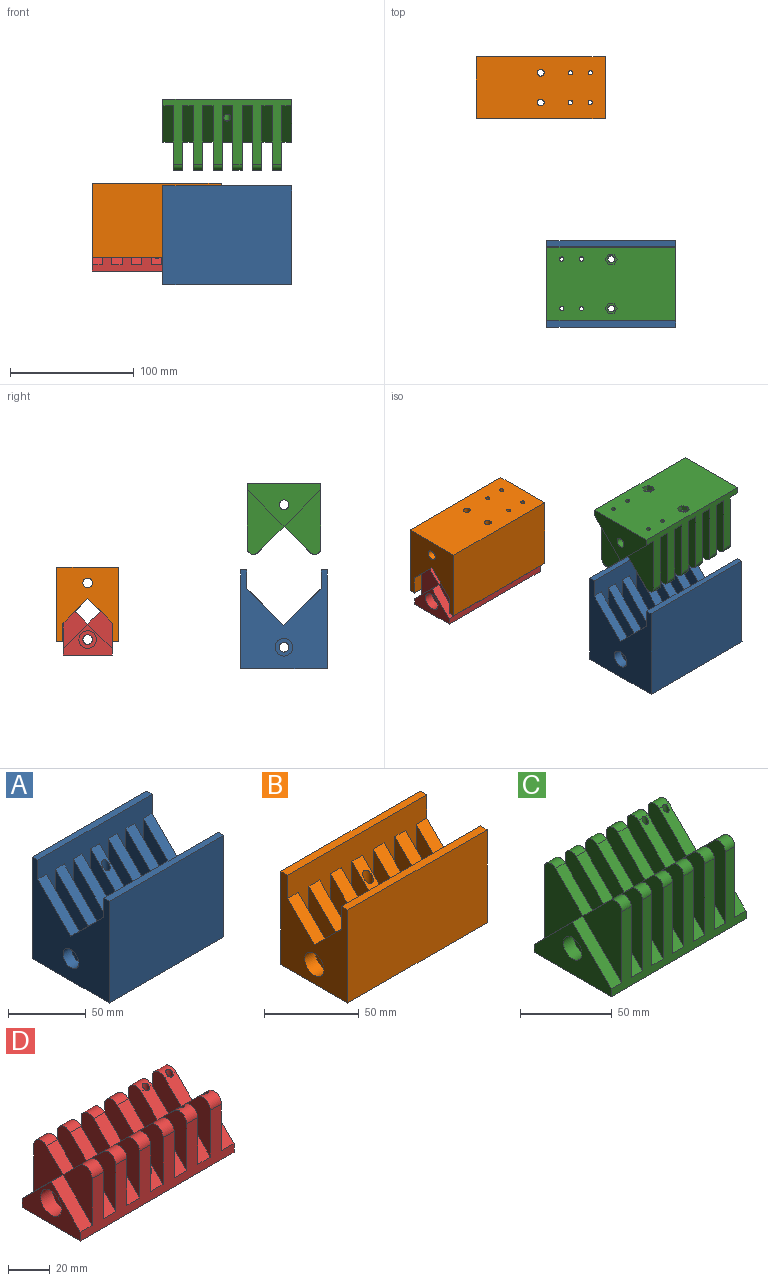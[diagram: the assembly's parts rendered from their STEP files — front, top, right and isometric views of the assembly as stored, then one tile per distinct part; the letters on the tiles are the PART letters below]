
ASSEMBLY  parts=4 mates=4
PART A: 68 faces, bbox 105.2x71.2x81.2 mm
  f0: plane 80x70mm, normal (-1,0,0), area 3640.5mm2, adj f1,f2,f4,f48,f49,f50,f51,f52
  f1: plane 104x70mm, normal (0,0,-1), area 7194mm2, adj f0,f50,f52,f56,f59,f60,f61,f62
  f2: plane 30x30mm, normal (0,-0.71,0.71), area 339.4mm2, adj f0,f3,f4,f48
  f3: plane 60x30mm, normal (1,0,0), area 900mm2, adj f2,f37,f48
  f4: plane 30x30mm, normal (0,0.71,0.71), area 339.4mm2, adj f0,f2,f5,f51
  f5: plane 60x30mm, normal (1,0,0), area 900mm2, adj f4,f36,f51
  f6: plane 30x30mm, normal (0,-0.71,0.71), area 339.4mm2, adj f7,f8,f9,f48
  f7: plane 60x30mm, normal (1,0,0), area 900mm2, adj f6,f39,f48
  f8: plane 60x30mm, normal (-1,0,0), area 900mm2, adj f6,f37,f48
  f9: plane 30x30mm, normal (0,0.71,0.71), area 339.4mm2, adj f6,f10,f11,f51
  f10: plane 60x30mm, normal (1,0,0), area 900mm2, adj f9,f38,f51
  f11: plane 60x30mm, normal (-1,0,0), area 900mm2, adj f9,f36,f51
  f12: plane 30x30mm, normal (0,-0.71,0.71), area 339.4mm2, adj f13,f14,f15,f48
  f13: plane 60x30mm, normal (1,0,0), area 900mm2, adj f12,f41,f48
  f14: plane 60x30mm, normal (-1,0,0), area 900mm2, adj f12,f39,f48
  f15: plane 30x30mm, normal (0,0.71,0.71), area 339.4mm2, adj f12,f16,f17,f51
  f16: plane 60x30mm, normal (1,0,0), area 900mm2, adj f15,f40,f51
  f17: plane 60x30mm, normal (-1,0,0), area 900mm2, adj f15,f38,f51
  f18: plane 31.16x31.16mm, normal (0,-0.71,0.71), area 305.8mm2, adj f19,f20,f21,f48,f64
  f19: plane 60x30mm, normal (1,0,0), area 900mm2, adj f18,f43,f48
  f20: plane 60x30mm, normal (-1,0,0), area 900mm2, adj f18,f41,f48
  f21: plane 31.16x31.16mm, normal (0,0.71,0.71), area 305.8mm2, adj f18,f22,f23,f51,f63
  f22: plane 60x30mm, normal (1,0,0), area 900mm2, adj f21,f42,f51
  f23: plane 60x30mm, normal (-1,0,0), area 900mm2, adj f21,f40,f51
  f24: plane 30x30mm, normal (0,-0.71,0.71), area 339.4mm2, adj f25,f26,f27,f48
  f25: plane 60x30mm, normal (1,0,0), area 900mm2, adj f24,f45,f48
  f26: plane 60x30mm, normal (-1,0,0), area 900mm2, adj f24,f43,f48
  f27: plane 30x30mm, normal (0,0.71,0.71), area 339.4mm2, adj f24,f28,f29,f51
  f28: plane 60x30mm, normal (1,0,0), area 900mm2, adj f27,f44,f51
  f29: plane 60x30mm, normal (-1,0,0), area 900mm2, adj f27,f42,f51
  f30: plane 30x30mm, normal (0,-0.71,0.71), area 339.4mm2, adj f31,f32,f33,f48
  f31: plane 60x30mm, normal (1,0,0), area 900mm2, adj f30,f47,f48
  f32: plane 60x30mm, normal (-1,0,0), area 900mm2, adj f30,f45,f48
  f33: plane 30x30mm, normal (0,0.71,0.71), area 339.4mm2, adj f30,f34,f35,f51
  f34: plane 60x30mm, normal (1,0,0), area 900mm2, adj f33,f46,f51
  f35: plane 60x30mm, normal (-1,0,0), area 900mm2, adj f33,f44,f51
  f36: plane 30.74x30.74mm, normal (0,-0.71,0.71), area 325.8mm2, adj f5,f11,f37,f51,f62
  f37: plane 30.74x30.74mm, normal (0,0.71,0.71), area 325.8mm2, adj f3,f8,f36,f48,f61
  f38: plane 30.74x30.74mm, normal (0,-0.71,0.71), area 325.8mm2, adj f10,f17,f39,f51,f60
  f39: plane 30.74x30.74mm, normal (0,0.71,0.71), area 325.8mm2, adj f7,f14,f38,f48,f59
  f40: plane 30x30mm, normal (0,-0.71,0.71), area 339.4mm2, adj f16,f23,f41,f51
  f41: plane 30x30mm, normal (0,0.71,0.71), area 339.4mm2, adj f13,f20,f40,f48
  f42: plane 30x30mm, normal (0,-0.71,0.71), area 339.4mm2, adj f22,f29,f43,f51
  f43: plane 30x30mm, normal (0,0.71,0.71), area 339.4mm2, adj f19,f26,f42,f48
  f44: plane 30x30mm, normal (0,-0.71,0.71), area 339.4mm2, adj f28,f35,f45,f51
  f45: plane 30x30mm, normal (0,0.71,0.71), area 339.4mm2, adj f25,f32,f44,f48
  f46: plane 30x30mm, normal (0,-0.71,0.71), area 339.4mm2, adj f34,f47,f51,f57
  f47: plane 30x30mm, normal (0,0.71,0.71), area 339.4mm2, adj f31,f46,f48,f54
  f48: plane 104x75mm, normal (0,-1,0), area 4440mm2, adj f0,f2,f3,f6,f7,f8,f12,f13
  f49: plane 104x5mm, normal (0,0,1), area 520mm2, adj f0,f48,f50,f56
  f50: plane 104x80mm, normal (0,1,0), area 8320mm2, adj f0,f1,f49,f56
  f51: plane 104x75mm, normal (0,1,0), area 4440mm2, adj f0,f4,f5,f9,f10,f11,f15,f16
  f52: plane 104x80mm, normal (0,-1,0), area 8320mm2, adj f0,f1,f53,f56
  f53: plane 104x5mm, normal (0,0,1), area 520mm2, adj f0,f51,f52,f56
  f54: plane 60x30mm, normal (-1,0,0), area 900mm2, adj f47,f48,f55
  f55: plane 30x30mm, normal (0,-0.71,0.71), area 339.4mm2, adj f48,f54,f56,f58
  f56: plane 80x70mm, normal (1,0,0), area 3752.2mm2, adj f1,f48,f49,f50,f51,f52,f53,f55
  f57: plane 60x30mm, normal (-1,0,0), area 900mm2, adj f46,f51,f58
  f58: plane 30x30mm, normal (0,0.71,0.71), area 339.4mm2, adj f51,f55,f56,f57
  f59: cylinder r=1.75mm len=16.85mm, axis (0,0,-1), area 166.5mm2, adj f1,f39
  f60: cylinder r=1.75mm len=16.76mm, axis (0,0,-1), area 165.6mm2, adj f1,f38
  f61: cylinder r=1.75mm len=16.76mm, axis (0,0,-1), area 165.6mm2, adj f1,f37
  f62: cylinder r=1.75mm len=16.76mm, axis (0,0,-1), area 165.6mm2, adj f1,f36
  f63: cylinder r=2.75mm len=57.76mm, axis (0,0,-1), area 952mm2, adj f1,f21
  f64: cylinder r=2.75mm len=57.76mm, axis (0,0,-1), area 952mm2, adj f1,f18
  f65: cylinder r=3.9mm len=96mm, axis (-1,0,0), area 2352.4mm2, adj f56,f66
  f66: plane 14.25x14.25mm, normal (-1,0,0), area 111.7mm2, adj f65,f67
  f67: cylinder r=7.12mm len=14.25mm, axis (-1,0,0), area 358.1mm2, adj f0,f66
PART B: 68 faces, bbox 105.2x51.2x61.2 mm
  f0: plane 60x50mm, normal (-1,0,0), area 1840.5mm2, adj f1,f2,f4,f48,f49,f50,f51,f52
  f1: plane 104x50mm, normal (0,0,-1), area 5114mm2, adj f0,f50,f52,f56,f59,f60,f61,f62
  f2: plane 20x20mm, normal (0,-0.71,0.71), area 226.3mm2, adj f0,f3,f4,f48
  f3: plane 40x20mm, normal (1,0,0), area 400mm2, adj f2,f37,f48
  f4: plane 20x20mm, normal (0,0.71,0.71), area 226.3mm2, adj f0,f2,f5,f51
  f5: plane 40x20mm, normal (1,0,0), area 400mm2, adj f4,f36,f51
  f6: plane 20x20mm, normal (0,-0.71,0.71), area 226.3mm2, adj f7,f8,f9,f48
  f7: plane 40x20mm, normal (1,0,0), area 400mm2, adj f6,f39,f48
  f8: plane 40x20mm, normal (-1,0,0), area 400mm2, adj f6,f37,f48
  f9: plane 20x20mm, normal (0,0.71,0.71), area 226.3mm2, adj f6,f10,f11,f51
  f10: plane 40x20mm, normal (1,0,0), area 400mm2, adj f9,f38,f51
  f11: plane 40x20mm, normal (-1,0,0), area 400mm2, adj f9,f36,f51
  f12: plane 20x20mm, normal (0,-0.71,0.71), area 226.3mm2, adj f13,f14,f15,f48
  f13: plane 40x20mm, normal (1,0,0), area 400mm2, adj f12,f41,f48
  f14: plane 40x20mm, normal (-1,0,0), area 400mm2, adj f12,f39,f48
  f15: plane 20x20mm, normal (0,0.71,0.71), area 226.3mm2, adj f12,f16,f17,f51
  f16: plane 40x20mm, normal (1,0,0), area 400mm2, adj f15,f40,f51
  f17: plane 40x20mm, normal (-1,0,0), area 400mm2, adj f15,f38,f51
  f18: plane 21.16x21.16mm, normal (0,-0.71,0.71), area 192.7mm2, adj f19,f20,f21,f48,f64
  f19: plane 40x20mm, normal (1,0,0), area 400mm2, adj f18,f43,f48
  f20: plane 40x20mm, normal (-1,0,0), area 400mm2, adj f18,f41,f48
  f21: plane 21.16x21.16mm, normal (0,0.71,0.71), area 192.7mm2, adj f18,f22,f23,f51,f63
  f22: plane 40x20mm, normal (1,0,0), area 400mm2, adj f21,f42,f51
  f23: plane 40x20mm, normal (-1,0,0), area 400mm2, adj f21,f40,f51
  f24: plane 20x20mm, normal (0,-0.71,0.71), area 226.3mm2, adj f25,f26,f27,f48
  f25: plane 40x20mm, normal (1,0,0), area 400mm2, adj f24,f45,f48
  f26: plane 40x20mm, normal (-1,0,0), area 400mm2, adj f24,f43,f48
  f27: plane 20x20mm, normal (0,0.71,0.71), area 226.3mm2, adj f24,f28,f29,f51
  f28: plane 40x20mm, normal (1,0,0), area 400mm2, adj f27,f44,f51
  f29: plane 40x20mm, normal (-1,0,0), area 400mm2, adj f27,f42,f51
  f30: plane 20x20mm, normal (0,-0.71,0.71), area 226.3mm2, adj f31,f32,f33,f48
  f31: plane 40x20mm, normal (1,0,0), area 400mm2, adj f30,f47,f48
  f32: plane 40x20mm, normal (-1,0,0), area 400mm2, adj f30,f45,f48
  f33: plane 20x20mm, normal (0,0.71,0.71), area 226.3mm2, adj f30,f34,f35,f51
  f34: plane 40x20mm, normal (1,0,0), area 400mm2, adj f33,f46,f51
  f35: plane 40x20mm, normal (-1,0,0), area 400mm2, adj f33,f44,f51
  f36: plane 20.74x20.74mm, normal (0,-0.71,0.71), area 212.7mm2, adj f5,f11,f37,f51,f62
  f37: plane 20.74x20.74mm, normal (0,0.71,0.71), area 212.7mm2, adj f3,f8,f36,f48,f61
  f38: plane 20.74x20.74mm, normal (0,-0.71,0.71), area 212.7mm2, adj f10,f17,f39,f51,f60
  f39: plane 20.74x20.74mm, normal (0,0.71,0.71), area 212.7mm2, adj f7,f14,f38,f48,f59
  f40: plane 20x20mm, normal (0,-0.71,0.71), area 226.3mm2, adj f16,f23,f41,f51
  f41: plane 20x20mm, normal (0,0.71,0.71), area 226.3mm2, adj f13,f20,f40,f48
  f42: plane 20x20mm, normal (0,-0.71,0.71), area 226.3mm2, adj f22,f29,f43,f51
  f43: plane 20x20mm, normal (0,0.71,0.71), area 226.3mm2, adj f19,f26,f42,f48
  f44: plane 20x20mm, normal (0,-0.71,0.71), area 226.3mm2, adj f28,f35,f45,f51
  f45: plane 20x20mm, normal (0,0.71,0.71), area 226.3mm2, adj f25,f32,f44,f48
  f46: plane 20x20mm, normal (0,-0.71,0.71), area 226.3mm2, adj f34,f47,f51,f57
  f47: plane 20x20mm, normal (0,0.71,0.71), area 226.3mm2, adj f31,f46,f48,f54
  f48: plane 104x55mm, normal (0,-1,0), area 3480mm2, adj f0,f2,f3,f6,f7,f8,f12,f13
  f49: plane 104x5mm, normal (0,0,1), area 520mm2, adj f0,f48,f50,f56
  f50: plane 104x60mm, normal (0,1,0), area 6240mm2, adj f0,f1,f49,f56
  f51: plane 104x55mm, normal (0,1,0), area 3480mm2, adj f0,f4,f5,f9,f10,f11,f15,f16
  f52: plane 104x60mm, normal (0,-1,0), area 6240mm2, adj f0,f1,f53,f56
  f53: plane 104x5mm, normal (0,0,1), area 520mm2, adj f0,f51,f52,f56
  f54: plane 40x20mm, normal (-1,0,0), area 400mm2, adj f47,f48,f55
  f55: plane 20x20mm, normal (0,-0.71,0.71), area 226.3mm2, adj f48,f54,f56,f58
  f56: plane 60x50mm, normal (1,0,0), area 1952.2mm2, adj f1,f48,f49,f50,f51,f52,f53,f55
  f57: plane 40x20mm, normal (-1,0,0), area 400mm2, adj f46,f51,f58
  f58: plane 20x20mm, normal (0,0.71,0.71), area 226.3mm2, adj f51,f55,f56,f57
  f59: cylinder r=1.75mm len=14.76mm, axis (0,0,-1), area 143.6mm2, adj f1,f39
  f60: cylinder r=1.75mm len=14.76mm, axis (0,0,-1), area 143.6mm2, adj f1,f38
  f61: cylinder r=1.75mm len=14.76mm, axis (0,0,-1), area 143.6mm2, adj f1,f37
  f62: cylinder r=1.75mm len=14.76mm, axis (0,0,-1), area 143.6mm2, adj f1,f36
  f63: cylinder r=2.75mm len=39.76mm, axis (0,0,-1), area 640.9mm2, adj f1,f21
  f64: cylinder r=2.75mm len=39.76mm, axis (0,0,-1), area 640.9mm2, adj f1,f18
  f65: cylinder r=3.9mm len=96mm, axis (-1,0,0), area 2352.4mm2, adj f56,f66
  f66: plane 14.25x14.25mm, normal (-1,0,0), area 111.7mm2, adj f65,f67
  f67: cylinder r=7.12mm len=14.25mm, axis (-1,0,0), area 358.1mm2, adj f0,f66
PART C: 90 faces, bbox 105.2x60.7x58.8 mm
  f0: cylinder r=5mm len=8.54mm, axis (1,0,0), area 87.1mm2, adj f19,f20,f21,f55,f70
  f1: cylinder r=5mm len=8.54mm, axis (1,0,0), area 87.1mm2, adj f22,f23,f24,f55,f69
  f2: cylinder r=5mm len=8.54mm, axis (-1,0,0), area 87.1mm2, adj f42,f43,f44,f54,f68
  f3: cylinder r=5mm len=8.54mm, axis (-1,0,0), area 87.1mm2, adj f45,f46,f47,f54,f67
  f4: plane 52.43x29.75mm, normal (-1,0,0), area 854.2mm2, adj f31,f54,f60,f65
  f5: plane 104x59.5mm, normal (0,0,-1), area 6033.1mm2, adj f7,f54,f55,f66,f67,f68,f69,f70
  f6: plane 52.43x29.75mm, normal (-1,0,0), area 854.2mm2, adj f8,f55,f56,f64
  f7: plane 59.5x35mm, normal (1,0,0), area 1149.7mm2, adj f5,f30,f53,f54,f55,f87
  f8: plane 21.21x21.21mm, normal (0,0.71,0.71), area 225mm2, adj f6,f9,f31,f56
  f9: plane 52.43x29.75mm, normal (1,0,0), area 854.2mm2, adj f8,f25,f55,f56
  f10: plane 21.21x21.21mm, normal (0,0.71,0.71), area 225mm2, adj f11,f12,f33,f57
  f11: plane 52.43x29.75mm, normal (1,0,0), area 854.2mm2, adj f10,f26,f55,f57
  f12: plane 52.43x29.75mm, normal (-1,0,0), area 854.2mm2, adj f10,f25,f55,f57
  f13: plane 21.21x21.21mm, normal (0,0.71,0.71), area 225mm2, adj f14,f15,f36,f58
  f14: plane 52.43x29.75mm, normal (1,0,0), area 854.2mm2, adj f13,f27,f55,f58
  f15: plane 52.43x29.75mm, normal (-1,0,0), area 854.2mm2, adj f13,f26,f55,f58
  f16: plane 21.21x21.21mm, normal (0,0.71,0.71), area 225mm2, adj f17,f18,f39,f59
  f17: plane 52.43x29.75mm, normal (1,0,0), area 854.2mm2, adj f16,f28,f55,f59
  f18: plane 52.43x29.75mm, normal (-1,0,0), area 854.2mm2, adj f16,f27,f55,f59
  f19: plane 21.31x21.31mm, normal (0,0.71,0.71), area 212.7mm2, adj f0,f20,f21,f42,f70
  f20: plane 52.43x29.75mm, normal (1,0,0), area 854.2mm2, adj f0,f19,f29,f55
  f21: plane 52.43x29.75mm, normal (-1,0,0), area 854.2mm2, adj f0,f19,f28,f55
  f22: plane 21.31x21.31mm, normal (0,0.71,0.71), area 212.7mm2, adj f1,f23,f24,f45,f69
  f23: plane 52.43x29.75mm, normal (1,0,0), area 854.2mm2, adj f1,f22,f30,f55
  f24: plane 52.43x29.75mm, normal (-1,0,0), area 854.2mm2, adj f1,f22,f29,f55
  f25: plane 29.75x29.75mm, normal (0,-0.71,0.71), area 357.6mm2, adj f9,f12,f48,f55
  f26: plane 29.75x29.75mm, normal (0,-0.71,0.71), area 357.6mm2, adj f11,f15,f49,f55
  f27: plane 30.91x30.91mm, normal (0,-0.71,0.71), area 324mm2, adj f14,f18,f50,f55,f85
  f28: plane 29.75x29.75mm, normal (0,-0.71,0.71), area 357.6mm2, adj f17,f21,f51,f55
  f29: plane 29.75x29.75mm, normal (0,-0.71,0.71), area 357.6mm2, adj f20,f24,f52,f55
  f30: plane 29.75x29.75mm, normal (0,-0.71,0.71), area 357.6mm2, adj f7,f23,f53,f55
  f31: plane 21.21x21.21mm, normal (0,-0.71,0.71), area 225mm2, adj f4,f8,f32,f60
  f32: plane 52.43x29.75mm, normal (1,0,0), area 854.2mm2, adj f31,f48,f54,f60
  f33: plane 21.21x21.21mm, normal (0,-0.71,0.71), area 225mm2, adj f10,f34,f35,f61
  f34: plane 52.43x29.75mm, normal (1,0,0), area 854.2mm2, adj f33,f49,f54,f61
  f35: plane 52.43x29.75mm, normal (-1,0,0), area 854.2mm2, adj f33,f48,f54,f61
  f36: plane 21.21x21.21mm, normal (0,-0.71,0.71), area 225mm2, adj f13,f37,f38,f62
  f37: plane 52.43x29.75mm, normal (1,0,0), area 854.2mm2, adj f36,f50,f54,f62
  f38: plane 52.43x29.75mm, normal (-1,0,0), area 854.2mm2, adj f36,f49,f54,f62
  f39: plane 21.21x21.21mm, normal (0,-0.71,0.71), area 225mm2, adj f16,f40,f41,f63
  f40: plane 52.43x29.75mm, normal (1,0,0), area 854.2mm2, adj f39,f51,f54,f63
  f41: plane 52.43x29.75mm, normal (-1,0,0), area 854.2mm2, adj f39,f50,f54,f63
  f42: plane 21.31x21.31mm, normal (0,-0.71,0.71), area 212.7mm2, adj f2,f19,f43,f44,f68
  f43: plane 52.43x29.75mm, normal (1,0,0), area 854.2mm2, adj f2,f42,f52,f54
  f44: plane 52.43x29.75mm, normal (-1,0,0), area 854.2mm2, adj f2,f42,f51,f54
  f45: plane 21.31x21.31mm, normal (0,-0.71,0.71), area 212.7mm2, adj f3,f22,f46,f47,f67
  f46: plane 52.43x29.75mm, normal (1,0,0), area 854.2mm2, adj f3,f45,f53,f54
  f47: plane 52.43x29.75mm, normal (-1,0,0), area 854.2mm2, adj f3,f45,f52,f54
  f48: plane 29.75x29.75mm, normal (0,0.71,0.71), area 357.6mm2, adj f25,f32,f35,f54
  f49: plane 29.75x29.75mm, normal (0,0.71,0.71), area 357.6mm2, adj f26,f34,f38,f54
  f50: plane 30.91x30.91mm, normal (0,0.71,0.71), area 324mm2, adj f27,f37,f41,f54,f86
  f51: plane 29.75x29.75mm, normal (0,0.71,0.71), area 357.6mm2, adj f28,f40,f44,f54
  f52: plane 29.75x29.75mm, normal (0,0.71,0.71), area 357.6mm2, adj f29,f43,f47,f54
  f53: plane 29.75x29.75mm, normal (0,0.71,0.71), area 357.6mm2, adj f7,f30,f46,f54
  f54: plane 104x52.68mm, normal (0,1,0), area 2680.3mm2, adj f2,f3,f4,f5,f7,f32,f34,f35
  f55: plane 104x52.68mm, normal (0,-1,0), area 2680.3mm2, adj f0,f1,f5,f6,f7,f9,f11,f12
  f56: cylinder r=5mm len=8.54mm, axis (1,0,0), area 88.4mm2, adj f6,f8,f9,f55
  f57: cylinder r=5mm len=8.54mm, axis (1,0,0), area 88.4mm2, adj f10,f11,f12,f55
  f58: cylinder r=5mm len=8.54mm, axis (1,0,0), area 88.4mm2, adj f13,f14,f15,f55
  f59: cylinder r=5mm len=8.54mm, axis (1,0,0), area 88.4mm2, adj f16,f17,f18,f55
  f60: cylinder r=5mm len=8.54mm, axis (-1,0,0), area 88.4mm2, adj f4,f31,f32,f54
  f61: cylinder r=5mm len=8.54mm, axis (-1,0,0), area 88.4mm2, adj f33,f34,f35,f54
  f62: cylinder r=5mm len=8.54mm, axis (-1,0,0), area 88.4mm2, adj f36,f37,f38,f54
  f63: cylinder r=5mm len=8.54mm, axis (-1,0,0), area 88.4mm2, adj f39,f40,f41,f54
  f64: plane 29.75x29.75mm, normal (0,-0.71,0.71), area 336.6mm2, adj f6,f55,f65,f66
  f65: plane 29.75x29.75mm, normal (0,0.71,0.71), area 336.6mm2, adj f4,f54,f64,f66
  f66: plane 59.5x35mm, normal (-1,0,0), area 1038mm2, adj f5,f54,f55,f64,f65,f89
  f67: cylinder r=1.75mm len=56.21mm, axis (0,0,-1), area 603.7mm2, adj f3,f5,f45
  f68: cylinder r=1.75mm len=56.21mm, axis (0,0,-1), area 603.7mm2, adj f2,f5,f42
  f69: cylinder r=1.75mm len=56.21mm, axis (0,0,-1), area 603.7mm2, adj f1,f5,f22
  f70: cylinder r=1.75mm len=56.21mm, axis (0,0,-1), area 603.7mm2, adj f0,f5,f19
  f71: plane 4.5x4.1mm, normal (-0.87,0.5,0), area 21.3mm2, adj f5,f72,f76,f77
  f72: plane 4.73x4.5mm, normal (0,1,0), area 21.3mm2, adj f5,f71,f73,f77
  f73: plane 4.5x4.1mm, normal (0.87,0.5,0), area 21.3mm2, adj f5,f72,f74,f77
  f74: plane 4.5x4.1mm, normal (0.87,-0.5,0), area 21.3mm2, adj f5,f73,f75,f77
  f75: plane 4.73x4.5mm, normal (0,-1,0), area 21.3mm2, adj f5,f74,f76,f77
  f76: plane 4.5x4.1mm, normal (-0.87,-0.5,0), area 21.3mm2, adj f5,f71,f75,f77
  f77: plane 9.47x8.2mm, normal (0,0,-1), area 34.5mm2, adj f71,f72,f73,f74,f75,f76,f86
  f78: plane 4.73x4.5mm, normal (0,1,0), area 21.3mm2, adj f5,f79,f83,f84
  f79: plane 4.5x4.1mm, normal (0.87,0.5,0), area 21.3mm2, adj f5,f78,f80,f84
  f80: plane 4.5x4.1mm, normal (0.87,-0.5,0), area 21.3mm2, adj f5,f79,f81,f84
  f81: plane 4.73x4.5mm, normal (0,-1,0), area 21.3mm2, adj f5,f80,f82,f84
  f82: plane 4.5x4.1mm, normal (-0.87,-0.5,0), area 21.3mm2, adj f5,f81,f83,f84
  f83: plane 4.5x4.1mm, normal (-0.87,0.5,0), area 21.3mm2, adj f5,f78,f82,f84
  f84: plane 9.47x8.2mm, normal (0,0,-1), area 34.5mm2, adj f78,f79,f80,f81,f82,f83,f85
  f85: cylinder r=2.75mm len=13.26mm, axis (0,0,-1), area 183mm2, adj f27,f84
  f86: cylinder r=2.75mm len=13.26mm, axis (0,0,-1), area 183mm2, adj f50,f77
  f87: cylinder r=3.9mm len=96mm, axis (-1,0,0), area 2352.4mm2, adj f7,f88
  f88: plane 14.25x14.25mm, normal (-1,0,0), area 111.7mm2, adj f87,f89
  f89: cylinder r=7.12mm len=14.25mm, axis (-1,0,0), area 358.1mm2, adj f66,f88
PART D: 90 faces, bbox 105.2x40.7x38.8 mm
  f0: cylinder r=5mm len=8.54mm, axis (1,0,0), area 79.7mm2, adj f19,f20,f21,f55,f70
  f1: cylinder r=5mm len=8.54mm, axis (1,0,0), area 79.7mm2, adj f22,f23,f24,f55,f69
  f2: cylinder r=5mm len=8.54mm, axis (-1,0,0), area 79.7mm2, adj f42,f43,f44,f54,f68
  f3: cylinder r=5mm len=8.54mm, axis (-1,0,0), area 79.7mm2, adj f45,f46,f47,f54,f67
  f4: plane 32.43x19.75mm, normal (-1,0,0), area 359.2mm2, adj f31,f54,f60,f65
  f5: plane 104x39.5mm, normal (0,0,-1), area 3953.1mm2, adj f7,f54,f55,f66,f67,f68,f69,f70
  f6: plane 32.43x19.75mm, normal (-1,0,0), area 359.2mm2, adj f8,f55,f56,f64
  f7: plane 39.5x25mm, normal (1,0,0), area 549.7mm2, adj f5,f30,f53,f54,f55,f87
  f8: plane 11.21x11.21mm, normal (0,0.71,0.71), area 118.9mm2, adj f6,f9,f31,f56
  f9: plane 32.43x19.75mm, normal (1,0,0), area 359.2mm2, adj f8,f25,f55,f56
  f10: plane 11.21x11.21mm, normal (0,0.71,0.71), area 118.9mm2, adj f11,f12,f33,f57
  f11: plane 32.43x19.75mm, normal (1,0,0), area 359.2mm2, adj f10,f26,f55,f57
  f12: plane 32.43x19.75mm, normal (-1,0,0), area 359.2mm2, adj f10,f25,f55,f57
  f13: plane 11.21x11.21mm, normal (0,0.71,0.71), area 118.9mm2, adj f14,f15,f36,f58
  f14: plane 32.43x19.75mm, normal (1,0,0), area 359.2mm2, adj f13,f27,f55,f58
  f15: plane 32.43x19.75mm, normal (-1,0,0), area 359.2mm2, adj f13,f26,f55,f58
  f16: plane 11.21x11.21mm, normal (0,0.71,0.71), area 118.9mm2, adj f17,f18,f39,f59
  f17: plane 32.43x19.75mm, normal (1,0,0), area 359.2mm2, adj f16,f28,f55,f59
  f18: plane 32.43x19.75mm, normal (-1,0,0), area 359.2mm2, adj f16,f27,f55,f59
  f19: plane 11.21x11.21mm, normal (0,0.71,0.71), area 115.9mm2, adj f0,f20,f21,f42,f70
  f20: plane 32.43x19.75mm, normal (1,0,0), area 359.2mm2, adj f0,f19,f29,f55
  f21: plane 32.43x19.75mm, normal (-1,0,0), area 359.2mm2, adj f0,f19,f28,f55
  f22: plane 11.21x11.21mm, normal (0,0.71,0.71), area 115.9mm2, adj f1,f23,f24,f45,f69
  f23: plane 32.43x19.75mm, normal (1,0,0), area 359.2mm2, adj f1,f22,f30,f55
  f24: plane 32.43x19.75mm, normal (-1,0,0), area 359.2mm2, adj f1,f22,f29,f55
  f25: plane 19.75x19.75mm, normal (0,-0.71,0.71), area 237.4mm2, adj f9,f12,f48,f55
  f26: plane 19.75x19.75mm, normal (0,-0.71,0.71), area 237.4mm2, adj f11,f15,f49,f55
  f27: plane 20.91x20.91mm, normal (0,-0.71,0.71), area 203.8mm2, adj f14,f18,f50,f55,f86
  f28: plane 19.75x19.75mm, normal (0,-0.71,0.71), area 237.4mm2, adj f17,f21,f51,f55
  f29: plane 19.75x19.75mm, normal (0,-0.71,0.71), area 237.4mm2, adj f20,f24,f52,f55
  f30: plane 19.75x19.75mm, normal (0,-0.71,0.71), area 237.4mm2, adj f7,f23,f53,f55
  f31: plane 11.21x11.21mm, normal (0,-0.71,0.71), area 118.9mm2, adj f4,f8,f32,f60
  f32: plane 32.43x19.75mm, normal (1,0,0), area 359.2mm2, adj f31,f48,f54,f60
  f33: plane 11.21x11.21mm, normal (0,-0.71,0.71), area 118.9mm2, adj f10,f34,f35,f61
  f34: plane 32.43x19.75mm, normal (1,0,0), area 359.2mm2, adj f33,f49,f54,f61
  f35: plane 32.43x19.75mm, normal (-1,0,0), area 359.2mm2, adj f33,f48,f54,f61
  f36: plane 11.21x11.21mm, normal (0,-0.71,0.71), area 118.9mm2, adj f13,f37,f38,f62
  f37: plane 32.43x19.75mm, normal (1,0,0), area 359.2mm2, adj f36,f50,f54,f62
  f38: plane 32.43x19.75mm, normal (-1,0,0), area 359.2mm2, adj f36,f49,f54,f62
  f39: plane 11.21x11.21mm, normal (0,-0.71,0.71), area 118.9mm2, adj f16,f40,f41,f63
  f40: plane 32.43x19.75mm, normal (1,0,0), area 359.2mm2, adj f39,f51,f54,f63
  f41: plane 32.43x19.75mm, normal (-1,0,0), area 359.2mm2, adj f39,f50,f54,f63
  f42: plane 11.21x11.21mm, normal (0,-0.71,0.71), area 115.9mm2, adj f2,f19,f43,f44,f68
  f43: plane 32.43x19.75mm, normal (1,0,0), area 359.2mm2, adj f2,f42,f52,f54
  f44: plane 32.43x19.75mm, normal (-1,0,0), area 359.2mm2, adj f2,f42,f51,f54
  f45: plane 11.21x11.21mm, normal (0,-0.71,0.71), area 115.9mm2, adj f3,f22,f46,f47,f67
  f46: plane 32.43x19.75mm, normal (1,0,0), area 359.2mm2, adj f3,f45,f53,f54
  f47: plane 32.43x19.75mm, normal (-1,0,0), area 359.2mm2, adj f3,f45,f52,f54
  f48: plane 19.75x19.75mm, normal (0,0.71,0.71), area 237.4mm2, adj f25,f32,f35,f54
  f49: plane 19.75x19.75mm, normal (0,0.71,0.71), area 237.4mm2, adj f26,f34,f38,f54
  f50: plane 20.91x20.91mm, normal (0,0.71,0.71), area 203.8mm2, adj f27,f37,f41,f54,f85
  f51: plane 19.75x19.75mm, normal (0,0.71,0.71), area 237.4mm2, adj f28,f40,f44,f54
  f52: plane 19.75x19.75mm, normal (0,0.71,0.71), area 237.4mm2, adj f29,f43,f47,f54
  f53: plane 19.75x19.75mm, normal (0,0.71,0.71), area 237.4mm2, adj f7,f30,f46,f54
  f54: plane 104x32.68mm, normal (0,1,0), area 1780.3mm2, adj f2,f3,f4,f5,f7,f32,f34,f35
  f55: plane 104x32.68mm, normal (0,-1,0), area 1780.3mm2, adj f0,f1,f5,f6,f7,f9,f11,f12
  f56: cylinder r=5mm len=8.54mm, axis (1,0,0), area 88.4mm2, adj f6,f8,f9,f55
  f57: cylinder r=5mm len=8.54mm, axis (1,0,0), area 88.4mm2, adj f10,f11,f12,f55
  f58: cylinder r=5mm len=8.54mm, axis (1,0,0), area 88.4mm2, adj f13,f14,f15,f55
  f59: cylinder r=5mm len=8.54mm, axis (1,0,0), area 88.4mm2, adj f16,f17,f18,f55
  f60: cylinder r=5mm len=8.54mm, axis (-1,0,0), area 88.4mm2, adj f4,f31,f32,f54
  f61: cylinder r=5mm len=8.54mm, axis (-1,0,0), area 88.4mm2, adj f33,f34,f35,f54
  f62: cylinder r=5mm len=8.54mm, axis (-1,0,0), area 88.4mm2, adj f36,f37,f38,f54
  f63: cylinder r=5mm len=8.54mm, axis (-1,0,0), area 88.4mm2, adj f39,f40,f41,f54
  f64: plane 19.75x19.75mm, normal (0,-0.71,0.71), area 223.4mm2, adj f6,f55,f65,f66
  f65: plane 19.75x19.75mm, normal (0,0.71,0.71), area 223.4mm2, adj f4,f54,f64,f66
  f66: plane 39.5x25mm, normal (-1,0,0), area 438mm2, adj f5,f54,f55,f64,f65,f89
  f67: cylinder r=1.75mm len=37.58mm, axis (0,0,-1), area 402.6mm2, adj f3,f5,f45
  f68: cylinder r=1.75mm len=37.58mm, axis (0,0,-1), area 402.6mm2, adj f2,f5,f42
  f69: cylinder r=1.75mm len=37.58mm, axis (0,0,-1), area 402.6mm2, adj f1,f5,f22
  f70: cylinder r=1.75mm len=37.58mm, axis (0,0,-1), area 402.6mm2, adj f0,f5,f19
  f71: plane 4.5x4.1mm, normal (-0.87,0.5,0), area 21.3mm2, adj f5,f72,f76,f77
  f72: plane 4.73x4.5mm, normal (0,1,0), area 21.3mm2, adj f5,f71,f73,f77
  f73: plane 4.5x4.1mm, normal (0.87,0.5,0), area 21.3mm2, adj f5,f72,f74,f77
  f74: plane 4.5x4.1mm, normal (0.87,-0.5,0), area 21.3mm2, adj f5,f73,f75,f77
  f75: plane 4.73x4.5mm, normal (0,-1,0), area 21.3mm2, adj f5,f74,f76,f77
  f76: plane 4.5x4.1mm, normal (-0.87,-0.5,0), area 21.3mm2, adj f5,f71,f75,f77
  f77: plane 9.47x8.2mm, normal (0,0,-1), area 34.5mm2, adj f71,f72,f73,f74,f75,f76,f85
  f78: plane 4.73x4.5mm, normal (0,1,0), area 21.3mm2, adj f5,f79,f83,f84
  f79: plane 4.5x4.1mm, normal (0.87,0.5,0), area 21.3mm2, adj f5,f78,f80,f84
  f80: plane 4.5x4.1mm, normal (0.87,-0.5,0), area 21.3mm2, adj f5,f79,f81,f84
  f81: plane 4.73x4.5mm, normal (0,-1,0), area 21.3mm2, adj f5,f80,f82,f84
  f82: plane 4.5x4.1mm, normal (-0.87,-0.5,0), area 21.3mm2, adj f5,f81,f83,f84
  f83: plane 4.5x4.1mm, normal (-0.87,0.5,0), area 21.3mm2, adj f5,f78,f82,f84
  f84: plane 9.47x8.2mm, normal (0,0,-1), area 34.5mm2, adj f78,f79,f80,f81,f82,f83,f86
  f85: cylinder r=2.75mm len=11.26mm, axis (0,0,-1), area 148.5mm2, adj f50,f77
  f86: cylinder r=2.75mm len=11.26mm, axis (0,0,-1), area 148.5mm2, adj f27,f84
  f87: cylinder r=3.9mm len=96mm, axis (-1,0,0), area 2352.4mm2, adj f7,f88
  f88: plane 14.25x14.25mm, normal (-1,0,0), area 111.7mm2, adj f87,f89
  f89: cylinder r=7.12mm len=14.25mm, axis (-1,0,0), area 358.1mm2, adj f66,f88
PLACE A rot(axis=(0,-0.98,-0.19),0deg) t=(37.15,22.25,-12.2)mm
PLACE B rot(axis=(0,1,0),180deg) t=(-11.85,180.94,69.8)mm
PLACE C rot(axis=(0,1,0),180deg) t=(37.15,22.16,138.03)mm
PLACE D t=(-11.85,180.94,-1.02)mm
MATE parallel C.f5 <-> A.f1  axis (0,0,1) through (41.35,22.16,138.03)mm
MATE slider D.f69 <-> B.f62  axis (0,0,-1) through (24.15,168.94,-1.02)mm
MATE slider C.f68 <-> A.f59  axis (0,0,1) through (17.15,42.16,138.03)mm
MATE planar A.f0 <-> C.f7  axis (-1,0,0) through (-10.85,22.25,17.04)mm
